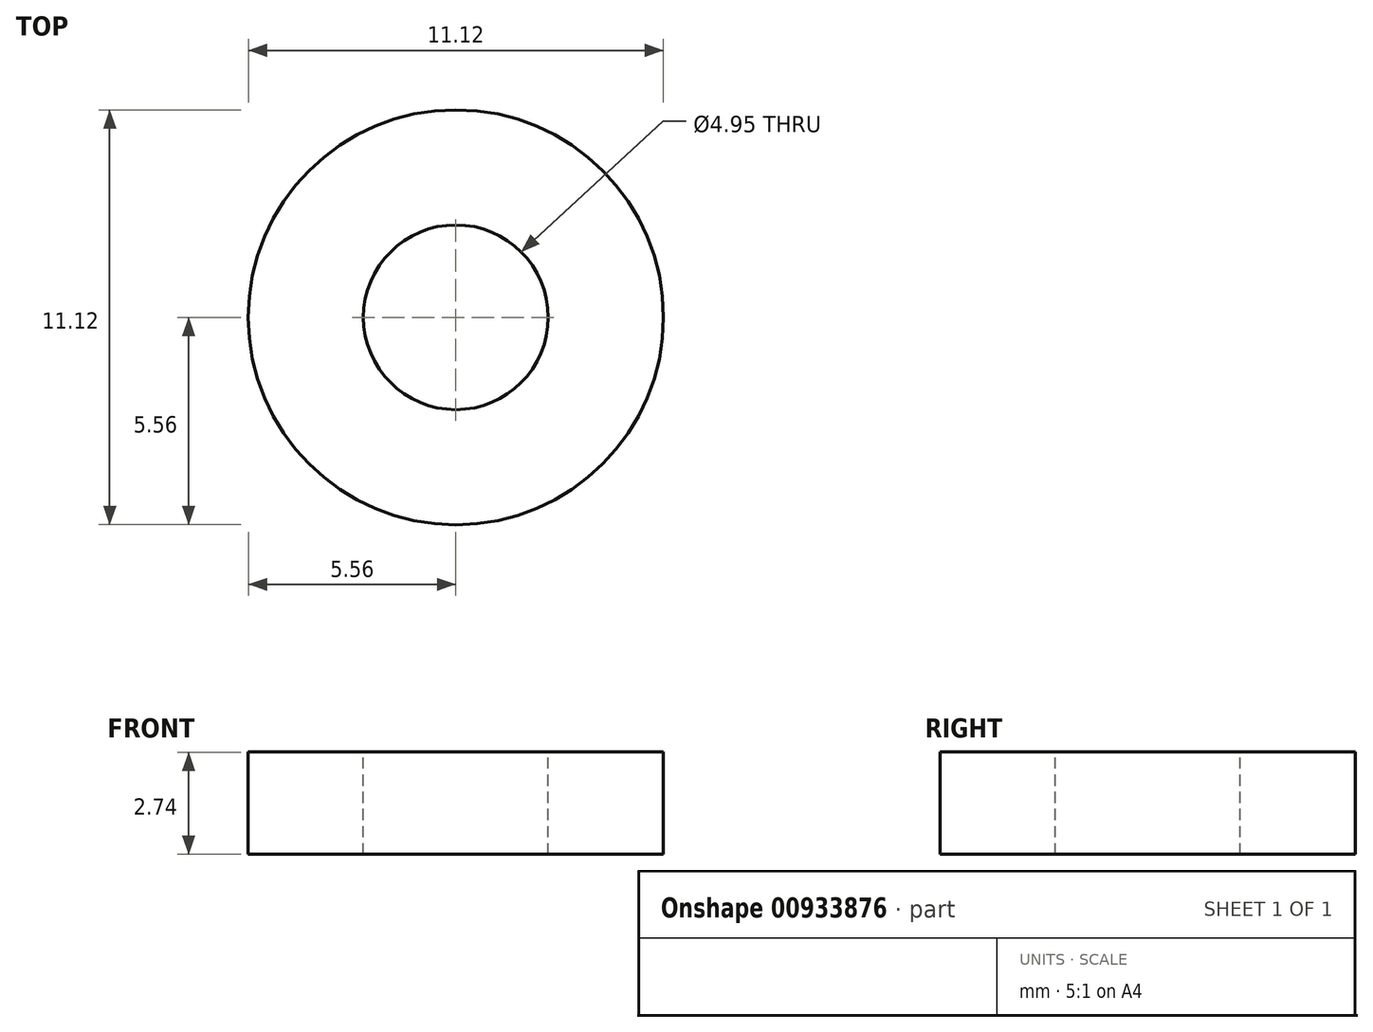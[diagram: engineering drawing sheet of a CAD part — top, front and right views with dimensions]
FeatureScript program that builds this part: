
annotation { "Feature Type Name" : "Feature", "Feature Type Description" : "" }
export const myFeature = defineFeature(function(context is Context, id is Id, definition is map)
    precondition{}
    {
        {
            var Q0;
            Q0=qCreatedBy(makeId("Front.planeOp"),FACE);
            var sketch = newSketch(context, id + "F0", { "sketchPlane" : qUnion([Q0])});
            skLineSegment(sketch, "E0", {"start": v(0, 32.77) * mm, "end": v(0, -32.77) * mm, "construction": true});
            skSolve(sketch);
        }
        {
            var Q0;
            Q0=qCreatedBy(makeId("Front.planeOp"),FACE);
            var sketch = newSketch(context, id + "F1", { "sketchPlane" : qUnion([Q0])});
            skLineSegment(sketch, "E1.bottom", {"start": v(5.56, 1.37) * mm, "end": v(2.48, 1.37) * mm});
            skLineSegment(sketch, "E1.top", {"start": v(5.56, -1.37) * mm, "end": v(2.48, -1.37) * mm});
            skLineSegment(sketch, "E1.left", {"start": v(5.56, 1.37) * mm, "end": v(5.56, -1.37) * mm});
            skLineSegment(sketch, "E1.right", {"start": v(2.48, 1.37) * mm, "end": v(2.48, -1.37) * mm});
            skPoint(sketch, "E1.middle", {"position": v(4.02, 0) * mm});
            skSolve(sketch);
        }
        {
            var Q0;
            Q0 = qSketchRegion(id + "F1", true);
            var Q1;
            Q1=sQuery(id+"F0.wireOp",EDGE,"E0");
            revolve(context, id + "F2", {"surfaceOperationType" : NewSurfaceOperationType.NEW, "entities" : qUnion([Q0]), "axis" : qUnion([Q1]), "revolveType" : RevolveType.FULL});
        }
    });
